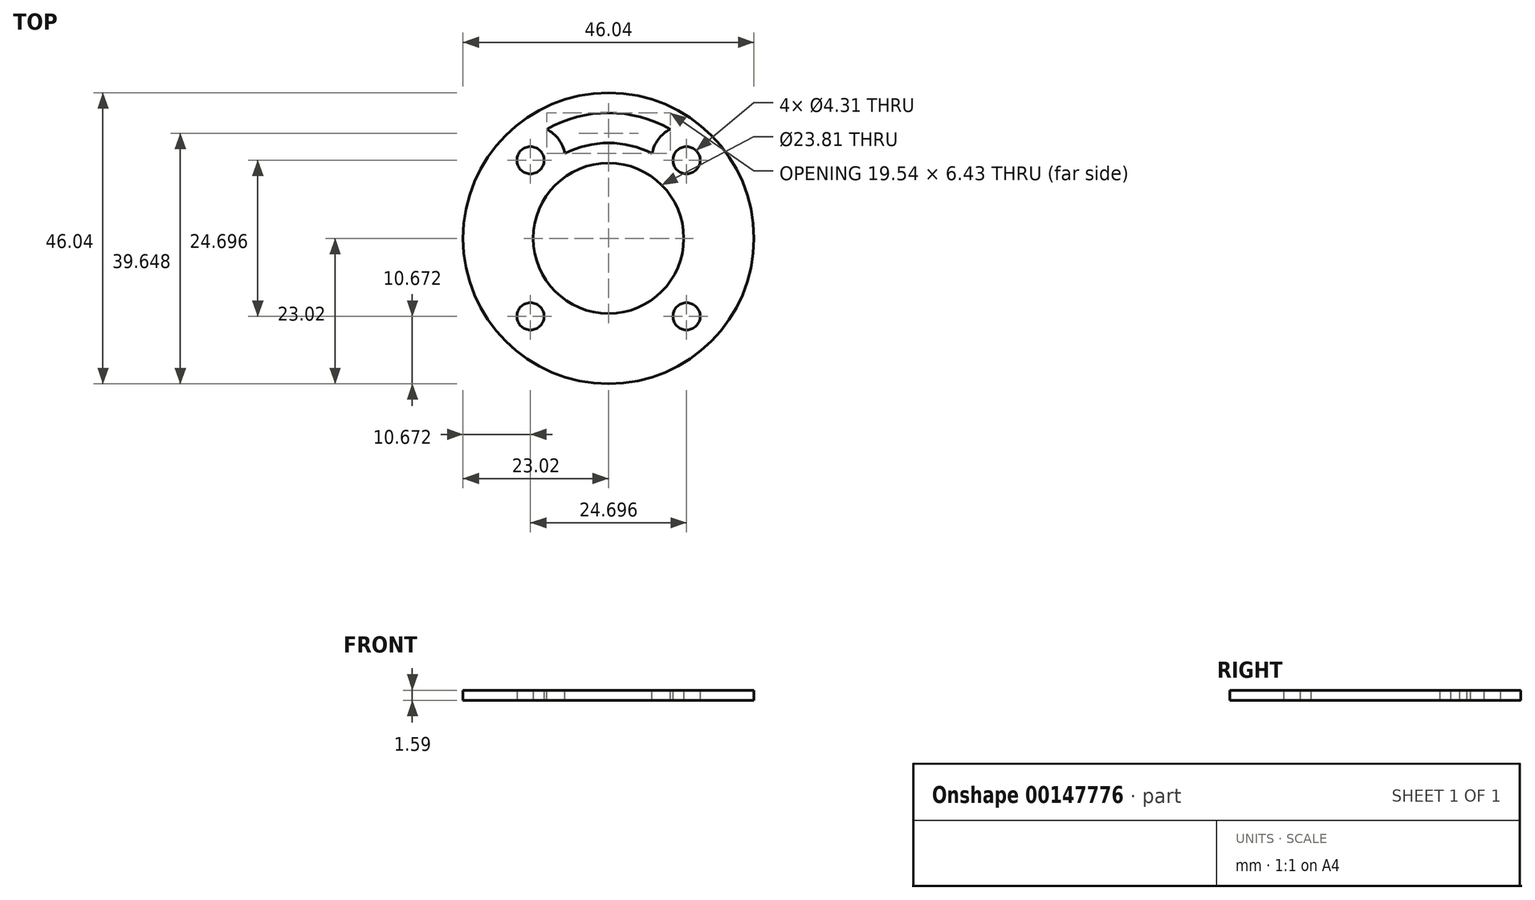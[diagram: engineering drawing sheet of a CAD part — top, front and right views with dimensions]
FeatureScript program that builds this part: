
annotation { "Feature Type Name" : "Feature", "Feature Type Description" : "" }
export const myFeature = defineFeature(function(context is Context, id is Id, definition is map)
    precondition{}
    {
        {
            var Q0;
            Q0=qCreatedBy(makeId("Top.planeOp"),FACE);
            var sketch = newSketch(context, id + "F0", { "sketchPlane" : qUnion([Q0])});
            skCircle(sketch, "E0", {"center": v(0, 0) * mm, "radius": 23.02 * mm});
            skCircle(sketch, "E1", {"center": v(0, 0) * mm, "radius": 11.9 * mm});
            skLineSegment(sketch, "E2.bottom", {"start": v(-12.35, 12.35) * mm, "end": v(12.35, 12.35) * mm, "construction": true});
            skLineSegment(sketch, "E2.top", {"start": v(-12.35, -12.35) * mm, "end": v(12.35, -12.35) * mm, "construction": true});
            skLineSegment(sketch, "E2.left", {"start": v(-12.35, 12.35) * mm, "end": v(-12.35, -12.35) * mm, "construction": true});
            skLineSegment(sketch, "E2.right", {"start": v(12.35, 12.35) * mm, "end": v(12.35, -12.35) * mm, "construction": true});
            skCircle(sketch, "E3", {"center": v(-12.35, 12.35) * mm, "radius": 5.56 * mm, "construction": true});
            skCircle(sketch, "E4", {"center": v(12.35, 12.35) * mm, "radius": 2.15 * mm});
            skCircle(sketch, "E5", {"center": v(-12.35, 12.35) * mm, "radius": 2.15 * mm});
            skCircle(sketch, "E6", {"center": v(-12.35, -12.35) * mm, "radius": 2.15 * mm});
            skCircle(sketch, "E7", {"center": v(12.35, -12.35) * mm, "radius": 2.15 * mm});
            skSolve(sketch);
        }
        {
            var Q0;
            Q0=qSketchRegion(id+"F0",true);
            extrude(context, id + "F1", {"entities" : qUnion([Q0]), "depth" : 1.59 * mm});
        }
        {
            var Q0;
            Q0=makeQuery(id+"F1.opExtrude","CAP_FACE",FACE,{"disambiguationData":[OSD([sQuery(id+"F0.wireOp",EDGE,"E0"),sQuery(id+"F0.wireOp",EDGE,"E1"),sQuery(id+"F0.wireOp",EDGE,"E4"),sQuery(id+"F0.wireOp",EDGE,"E5"),sQuery(id+"F0.wireOp",EDGE,"E6"),sQuery(id+"F0.wireOp",EDGE,"E7")])],"isStart":false});
            var sketch = newSketch(context, id + "F2", { "sketchPlane" : qUnion([Q0])});
            skArc(sketch, "E8", {"start": v(-6.9, 13.41) * mm, "mid": v(-7.9, 15.67) * mm, "end": v(-9.77, 17.27) * mm});
            skArc(sketch, "E9", {"start": v(9.77, 17.27) * mm, "mid": v(0, 19.84) * mm, "end": v(-9.77, 17.27) * mm});
            skArc(sketch, "E10", {"start": v(6.9, 13.41) * mm, "mid": v(0, 15.08) * mm, "end": v(-6.9, 13.41) * mm});
            skArc(sketch, "E11", {"start": v(9.77, 17.27) * mm, "mid": v(7.9, 15.67) * mm, "end": v(6.9, 13.41) * mm});
            skSolve(sketch);
        }
        {
            var Q0;
            Q0=qSketchRegion(id+"F2",true);
            var Q1;
            Q1=makeQuery(id+"F1.opExtrude","CAP_FACE",FACE,{"disambiguationData":[OSD([sQuery(id+"F0.wireOp",EDGE,"E0"),sQuery(id+"F0.wireOp",EDGE,"E1"),sQuery(id+"F0.wireOp",EDGE,"E4"),sQuery(id+"F0.wireOp",EDGE,"E5"),sQuery(id+"F0.wireOp",EDGE,"E6"),sQuery(id+"F0.wireOp",EDGE,"E7")])],"isStart":true});
            extrude(context, id + "F3", {"entities" : qUnion([Q0]), "operationType" : NewBodyOperationType.REMOVE, "endBound" : BoundingType.UP_TO_SURFACE, "oppositeDirection" : true, "endBoundEntityFace" : qUnion([Q1]), "depth" : 25.4 * mm});
        }
    });
